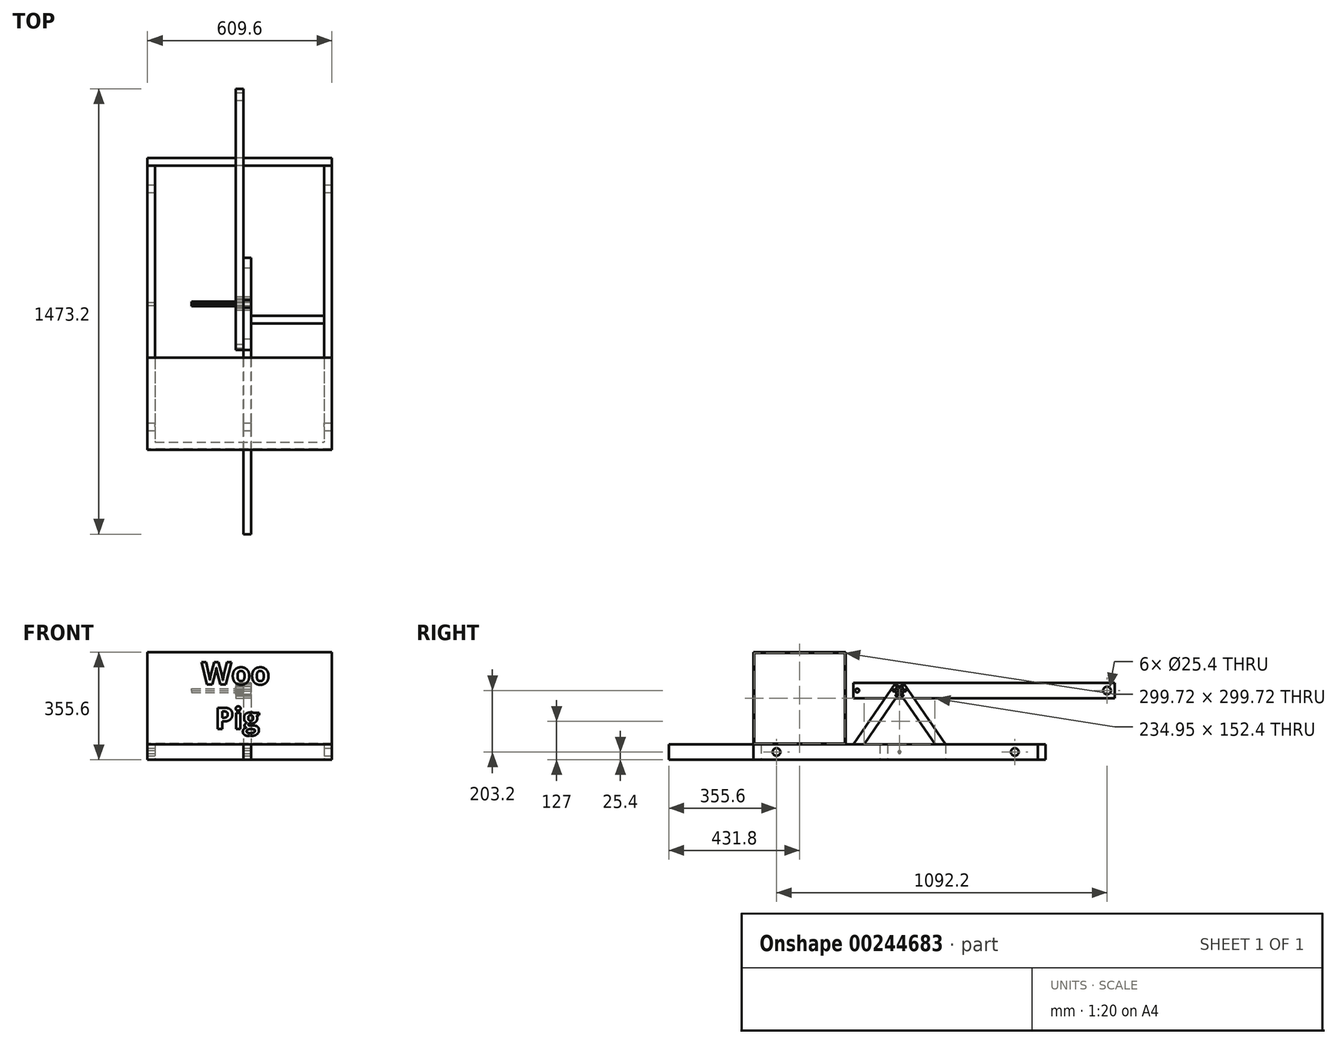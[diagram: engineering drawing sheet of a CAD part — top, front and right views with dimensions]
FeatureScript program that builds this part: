
annotation { "Feature Type Name" : "Feature", "Feature Type Description" : "" }
export const myFeature = defineFeature(function(context is Context, id is Id, definition is map)
    precondition{}
    {
        {
            var Q0;
            Q0=qCreatedBy(makeId("Top.planeOp"),FACE);
            var sketch = newSketch(context, id + "F0", { "sketchPlane" : qUnion([Q0])});
            skLineSegment(sketch, "E0.bottom", {"start": v(0, 863.6) * mm, "end": v(25.4, 863.6) * mm});
            skLineSegment(sketch, "E0.top", {"start": v(0, 0) * mm, "end": v(25.4, 0) * mm});
            skLineSegment(sketch, "E0.left", {"start": v(0, 863.6) * mm, "end": v(0, 0) * mm});
            skLineSegment(sketch, "E0.right", {"start": v(25.4, 863.6) * mm, "end": v(25.4, 0) * mm});
            skSolve(sketch);
        }
        {
            var Q0;
            Q0=makeQuery(id+"F0.imprint","IMPRINT",FACE,{"disambiguationData":[TD([[makeQuery(id+"F0.imprint","IMPRINT",EDGE,{"derivedFrom":sQuery(id+"F0.wireOp",EDGE,"E0.bottom")}),-1.0]])]});
            extrude(context, id + "F1", {"entities" : qUnion([Q0]), "depth" : 50.8 * mm});
        }
        {
            var Q0;
            Q0=makeQuery(id+"F1.opExtrude","SWEPT_FACE",FACE,{"disambiguationData":[OSD([sQuery(id+"F0.wireOp",EDGE,"E0.right")])]});
            var sketch = newSketch(context, id + "F2", { "sketchPlane" : qUnion([Q0])});
            skLineSegment(sketch, "E1", {"start": v(0, 25.4) * mm, "end": v(863.6, 25.4) * mm, "construction": true});
            skCircle(sketch, "E2", {"center": v(152.4, 25.4) * mm, "radius": 12.7 * mm, "construction": true});
            skCircle(sketch, "E3", {"center": v(838.2, 25.4) * mm, "radius": 12.7 * mm});
            skCircle(sketch, "E4", {"center": v(12.7, 25.4) * mm, "radius": 6.35 * mm});
            skSolve(sketch);
        }
        {
            var Q0;
            Q0=qSketchRegion(id+"F2",true);
            extrude(context, id + "F3", {"entities" : qUnion([Q0]), "operationType" : NewBodyOperationType.REMOVE, "endBound" : BoundingType.THROUGH_ALL, "oppositeDirection" : true, "depth" : 25.4 * mm});
        }
        {
            var Q0;
            Q0=makeQuery(id+"F1.opExtrude","SWEPT_FACE",FACE,{"disambiguationData":[OSD([sQuery(id+"F0.wireOp",EDGE,"E0.right")])]});
            var sketch = newSketch(context, id + "F4", { "sketchPlane" : qUnion([Q0])});
            skLineSegment(sketch, "E5", {"start": v(152.4, 50.8) * mm, "end": v(139.7, 50.8) * mm, "construction": true});
            skLineSegment(sketch, "E6", {"start": v(139.7, 50.8) * mm, "end": v(139.7, 0) * mm, "construction": true});
            skLineSegment(sketch, "E7", {"start": v(165.1, 50.8) * mm, "end": v(165.1, 0) * mm, "construction": true});
            skLineSegment(sketch, "E8", {"start": v(139.7, 50.8) * mm, "end": v(0, -152.4) * mm});
            skLineSegment(sketch, "E9", {"start": v(139.7, 0) * mm, "end": v(34.92, -152.4) * mm});
            skLineSegment(sketch, "E10", {"start": v(139.7, 0) * mm, "end": v(139.7, -152.4) * mm, "construction": true});
            skLineSegment(sketch, "E11", {"start": v(139.7, -152.4) * mm, "end": v(-61.1, -152.4) * mm, "construction": true});
            skLineSegment(sketch, "E12", {"start": v(0, -152.4) * mm, "end": v(-609.6, -152.4) * mm});
            skLineSegment(sketch, "E13", {"start": v(-609.6, -152.4) * mm, "end": v(-609.6, -203.2) * mm});
            skLineSegment(sketch, "E14", {"start": v(-609.6, -203.2) * mm, "end": v(139.7, -203.2) * mm});
            skLineSegment(sketch, "E15", {"start": v(34.92, -152.4) * mm, "end": v(139.7, -152.4) * mm});
            skLineSegment(sketch, "E16", {"start": v(152.4, 50.8) * mm, "end": v(152.4, -203.2) * mm, "construction": true});
            skLineSegment(sketch, "E17", {"start": v(139.7, 50.8) * mm, "end": v(152.4, 50.8) * mm});
            skLineSegment(sketch, "E18.MirrorCS", {"start": v(165.1, 0) * mm, "end": v(269.88, -152.4) * mm});
            skLineSegment(sketch, "E19.MirrorCS", {"start": v(165.1, 50.8) * mm, "end": v(304.8, -152.4) * mm});
            skLineSegment(sketch, "E20.MirrorCS", {"start": v(165.1, -152.4) * mm, "end": v(365.9, -152.4) * mm, "construction": true});
            skLineSegment(sketch, "E21.MirrorCS", {"start": v(152.4, 50.8) * mm, "end": v(165.1, 50.8) * mm, "construction": true});
            skLineSegment(sketch, "E22", {"start": v(139.7, -152.4) * mm, "end": v(269.88, -152.4) * mm});
            skLineSegment(sketch, "E23", {"start": v(139.7, -203.2) * mm, "end": v(165.1, -203.2) * mm});
            skLineSegment(sketch, "E24", {"start": v(139.7, 0) * mm, "end": v(165.1, 0) * mm});
            skLineSegment(sketch, "E25", {"start": v(152.4, 50.8) * mm, "end": v(165.1, 50.8) * mm});
            skLineSegment(sketch, "E26", {"start": v(304.8, -152.4) * mm, "end": v(304.8, -203.2) * mm});
            skLineSegment(sketch, "E27", {"start": v(304.8, -203.2) * mm, "end": v(165.1, -203.2) * mm});
            skLineSegment(sketch, "E28", {"start": v(165.1, -152.4) * mm, "end": v(269.88, -152.4) * mm});
            skSolve(sketch);
        }
        {
            var Q0;
            {var subQ0=sQuery(id+"F4.wireOp",EDGE,"E9");Q0=makeQuery(id+"F4.imprint","IMPRINT",FACE,{"disambiguationData":[TD([[makeQuery(id+"F4.imprint","IMPRINT",EDGE,{"derivedFrom":subQ0}),-1.0]])]});}
            var Q1;
            {var subQ7=sQuery(id+"F4.wireOp",EDGE,"E17");Q1=makeQuery(id+"F4.imprint","IMPRINT",FACE,{"disambiguationData":[TD([[makeQuery(id+"F4.imprint","IMPRINT",EDGE,{"derivedFrom":subQ7}),1.0]])]});}
            extrude(context, id + "F5", {"entities" : qUnion([Q0, Q1]), "depth" : 25.4 * mm});
        }
        {
            var Q0;
            Q0=qCreatedBy(makeId("Front.planeOp"),FACE);
            cPlane(context, id + "F6", {"entities" : qUnion([Q0]), "cplaneType" : CPlaneType.OFFSET, "offset" : 304.8 * mm, "width" : 152.4 * mm, "height" : 152.4 * mm});
        }
        {
            var Q0;
            Q0=qCreatedBy(id+"F6.planeOp",FACE);
            var sketch = newSketch(context, id + "F7", { "sketchPlane" : qUnion([Q0])});
            skLineSegment(sketch, "E29", {"start": v(0, 0) * mm, "end": v(0, -319.22) * mm, "construction": true});
            skLineSegment(sketch, "E30", {"start": v(12.7, 0) * mm, "end": v(12.7, -203.2) * mm, "construction": true});
            skLineSegment(sketch, "E31.bottom", {"start": v(-292.1, -152.4) * mm, "end": v(317.5, -152.4) * mm});
            skLineSegment(sketch, "E31.top", {"start": v(-292.1, -203.2) * mm, "end": v(317.5, -203.2) * mm});
            skLineSegment(sketch, "E31.left", {"start": v(-292.1, -152.4) * mm, "end": v(-292.1, -203.2) * mm});
            skLineSegment(sketch, "E31.right", {"start": v(317.5, -152.4) * mm, "end": v(317.5, -203.2) * mm});
            skLineSegment(sketch, "E32", {"start": v(-27.3, -203.2) * mm, "end": v(60.07, -203.2) * mm, "construction": true});
            skSolve(sketch);
        }
        {
            var Q0;
            Q0=makeQuery(id+"F7.imprint","IMPRINT",FACE,{"disambiguationData":[TD([[makeQuery(id+"F7.imprint","IMPRINT",EDGE,{"derivedFrom":sQuery(id+"F7.wireOp",EDGE,"E31.bottom")}),-1.0]])]});
            extrude(context, id + "F8", {"entities" : qUnion([Q0]), "depth" : 25.4 * mm});
        }
        {
            var Q0;
            Q0=makeQuery(id+"F8.opExtrude","CAP_FACE",FACE,{"disambiguationData":[OSD([sQuery(id+"F7.wireOp",EDGE,"E31.bottom"),sQuery(id+"F7.wireOp",EDGE,"E31.top"),sQuery(id+"F7.wireOp",EDGE,"E31.left"),sQuery(id+"F7.wireOp",EDGE,"E31.right")])],"isStart":true});
            var sketch = newSketch(context, id + "F9", { "sketchPlane" : qUnion([Q0])});
            skLineSegment(sketch, "E33.bottom", {"start": v(-317.5, -152.4) * mm, "end": v(-292.1, -152.4) * mm});
            skLineSegment(sketch, "E33.top", {"start": v(-317.5, -203.2) * mm, "end": v(-292.1, -203.2) * mm});
            skLineSegment(sketch, "E33.left", {"start": v(-317.5, -152.4) * mm, "end": v(-317.5, -203.2) * mm});
            skLineSegment(sketch, "E33.right", {"start": v(-292.1, -152.4) * mm, "end": v(-292.1, -203.2) * mm});
            skSolve(sketch);
        }
        {
            var Q0;
            Q0=makeQuery(id+"F9.imprint","IMPRINT",FACE,{"disambiguationData":[TD([[makeQuery(id+"F9.imprint","IMPRINT",EDGE,{"derivedFrom":sQuery(id+"F9.wireOp",EDGE,"E33.bottom")}),1.0]])]});
            extrude(context, id + "F10", {"entities" : qUnion([Q0]), "operationType" : NewBodyOperationType.ADD, "depth" : 914.4 * mm});
        }
        {
            var Q0;
            Q0=makeQuery(id+"F8.opExtrude","CAP_FACE",FACE,{"disambiguationData":[OSD([sQuery(id+"F7.wireOp",EDGE,"E31.bottom"),sQuery(id+"F7.wireOp",EDGE,"E31.top"),sQuery(id+"F7.wireOp",EDGE,"E31.left"),sQuery(id+"F7.wireOp",EDGE,"E31.right")])],"isStart":true});
            var sketch = newSketch(context, id + "F11", { "sketchPlane" : qUnion([Q0])});
            skLineSegment(sketch, "E34.bottom", {"start": v(292.1, -152.4) * mm, "end": v(266.7, -152.4) * mm});
            skLineSegment(sketch, "E34.top", {"start": v(292.1, -203.2) * mm, "end": v(266.7, -203.2) * mm});
            skLineSegment(sketch, "E34.left", {"start": v(292.1, -152.4) * mm, "end": v(292.1, -203.2) * mm});
            skLineSegment(sketch, "E34.right", {"start": v(266.7, -152.4) * mm, "end": v(266.7, -203.2) * mm});
            skSolve(sketch);
        }
        {
            var Q0;
            Q0=makeQuery(id+"F11.imprint","IMPRINT",FACE,{"disambiguationData":[TD([[makeQuery(id+"F11.imprint","IMPRINT",EDGE,{"derivedFrom":sQuery(id+"F11.wireOp",EDGE,"E34.bottom")}),1.0]])]});
            extrude(context, id + "F12", {"entities" : qUnion([Q0]), "operationType" : NewBodyOperationType.ADD, "depth" : 914.4 * mm});
        }
        {
            var Q0;
            Q0=makeQuery(id+"F10.opExtrude","CAP_FACE",FACE,{"disambiguationData":[OSD([sQuery(id+"F9.wireOp",EDGE,"E33.bottom"),sQuery(id+"F9.wireOp",EDGE,"E33.top"),sQuery(id+"F9.wireOp",EDGE,"E33.left"),sQuery(id+"F9.wireOp",EDGE,"E33.right")])],"isStart":false});
            var sketch = newSketch(context, id + "F13", { "sketchPlane" : qUnion([Q0])});
            skLineSegment(sketch, "E35.bottom", {"start": v(-317.5, -152.4) * mm, "end": v(292.1, -152.4) * mm});
            skLineSegment(sketch, "E35.top", {"start": v(-317.5, -203.2) * mm, "end": v(292.1, -203.2) * mm});
            skLineSegment(sketch, "E35.left", {"start": v(-317.5, -152.4) * mm, "end": v(-317.5, -203.2) * mm});
            skLineSegment(sketch, "E35.right", {"start": v(292.1, -152.4) * mm, "end": v(292.1, -203.2) * mm});
            skSolve(sketch);
        }
        {
            var Q0;
            Q0=qSketchRegion(id+"F13",true);
            extrude(context, id + "F14", {"entities" : qUnion([Q0]), "depth" : 25.4 * mm});
        }
        {
            var Q0;
            Q0=makeQuery(id+"F10.boolean.opBoolean","MERGE",FACE,{"derivedFrom":[makeQuery(id+"F8.opExtrude","SWEPT_FACE",FACE,{"disambiguationData":[OSD([sQuery(id+"F7.wireOp",EDGE,"E31.right")])]}),makeQuery(id+"F10.opExtrude","SWEPT_FACE",FACE,{"disambiguationData":[OSD([sQuery(id+"F9.wireOp",EDGE,"E33.left")])]})]});
            var sketch = newSketch(context, id + "F15", { "sketchPlane" : qUnion([Q0])});
            skLineSegment(sketch, "E36.bottom", {"start": v(-330.2, -152.4) * mm, "end": v(609.6, -152.4) * mm, "construction": true});
            skLineSegment(sketch, "E36.top", {"start": v(-330.2, -203.2) * mm, "end": v(609.6, -203.2) * mm, "construction": true});
            skLineSegment(sketch, "E36.left", {"start": v(-330.2, -152.4) * mm, "end": v(-330.2, -203.2) * mm, "construction": true});
            skLineSegment(sketch, "E36.right", {"start": v(609.6, -152.4) * mm, "end": v(609.6, -203.2) * mm, "construction": true});
            skLineSegment(sketch, "E37", {"start": v(609.6, -177.8) * mm, "end": v(-330.2, -177.8) * mm, "construction": true});
            skCircle(sketch, "E38", {"center": v(-254, -177.8) * mm, "radius": 12.7 * mm});
            skLineSegment(sketch, "E39", {"start": v(139.7, -152.4) * mm, "end": v(139.7, -203.2) * mm, "construction": true});
            skCircle(sketch, "E40.MirrorC", {"center": v(533.4, -177.8) * mm, "radius": 12.7 * mm});
            skSolve(sketch);
        }
        {
            var Q0;
            Q0=qSketchRegion(id+"F15",true);
            extrude(context, id + "F16", {"entities" : qUnion([Q0]), "operationType" : NewBodyOperationType.REMOVE, "endBound" : BoundingType.THROUGH_ALL, "oppositeDirection" : true, "depth" : 25.4 * mm});
        }
        {
            var Q0;
            Q0=makeQuery(id+"F12.boolean.opBoolean","MERGE",FACE,{"derivedFrom":[makeQuery(id+"F10.boolean.opBoolean","MERGE",FACE,{"derivedFrom":[makeQuery(id+"F8.opExtrude","SWEPT_FACE",FACE,{"disambiguationData":[OSD([sQuery(id+"F7.wireOp",EDGE,"E31.top")])]}),makeQuery(id+"F10.opExtrude","SWEPT_FACE",FACE,{"disambiguationData":[OSD([sQuery(id+"F9.wireOp",EDGE,"E33.top")])]})]}),makeQuery(id+"F12.opExtrude","SWEPT_FACE",FACE,{"disambiguationData":[OSD([sQuery(id+"F11.wireOp",EDGE,"E34.top")])]})]});
            var sketch = newSketch(context, id + "F17", { "sketchPlane" : qUnion([Q0])});
            skLineSegment(sketch, "E41.bottom", {"start": v(292.1, -87.93) * mm, "end": v(50.8, -87.93) * mm});
            skLineSegment(sketch, "E41.top", {"start": v(292.1, -113.33) * mm, "end": v(50.8, -113.33) * mm});
            skLineSegment(sketch, "E41.left", {"start": v(292.1, -87.93) * mm, "end": v(292.1, -113.33) * mm});
            skLineSegment(sketch, "E41.right", {"start": v(50.8, -87.93) * mm, "end": v(50.8, -113.33) * mm});
            skSolve(sketch);
        }
        {
            var Q0;
            Q0=makeQuery(id+"F17.imprint","IMPRINT",FACE,{"disambiguationData":[TD([[makeQuery(id+"F17.imprint","IMPRINT",EDGE,{"derivedFrom":sQuery(id+"F17.wireOp",EDGE,"E41.bottom")}),1.0]])]});
            extrude(context, id + "F18", {"entities" : qUnion([Q0]), "oppositeDirection" : true, "depth" : 50.8 * mm});
        }
        {
            var Q0;
            Q0=makeQuery(id+"F12.boolean.opBoolean","MERGE",FACE,{"derivedFrom":[makeQuery(id+"F8.opExtrude","SWEPT_FACE",FACE,{"disambiguationData":[OSD([sQuery(id+"F7.wireOp",EDGE,"E31.left")])]}),makeQuery(id+"F12.opExtrude","SWEPT_FACE",FACE,{"disambiguationData":[OSD([sQuery(id+"F11.wireOp",EDGE,"E34.left")])]})]});
            var sketch = newSketch(context, id + "F19", { "sketchPlane" : qUnion([Q0])});
            skLineSegment(sketch, "E42.bottom", {"start": v(330.2, -152.4) * mm, "end": v(25.4, -152.4) * mm});
            skLineSegment(sketch, "E42.top", {"start": v(330.2, 152.4) * mm, "end": v(25.4, 152.4) * mm});
            skLineSegment(sketch, "E42.left", {"start": v(330.2, -152.4) * mm, "end": v(330.2, 152.4) * mm});
            skLineSegment(sketch, "E42.right", {"start": v(25.4, -152.4) * mm, "end": v(25.4, 152.4) * mm});
            skSolve(sketch);
        }
        {
            var Q0;
            Q0=makeQuery(id+"F19.imprint","IMPRINT",FACE,{"disambiguationData":[TD([[makeQuery(id+"F19.imprint","IMPRINT",EDGE,{"derivedFrom":sQuery(id+"F19.wireOp",EDGE,"E42.bottom")}),-1.0]])]});
            extrude(context, id + "F20", {"entities" : qUnion([Q0]), "oppositeDirection" : true, "depth" : 609.6 * mm});
        }
        {
            var Q0;
            Q0=makeQuery(id+"F20.opExtrude","CAP_FACE",FACE,{"disambiguationData":[OSD([sQuery(id+"F19.wireOp",EDGE,"E42.bottom"),sQuery(id+"F19.wireOp",EDGE,"E42.top"),sQuery(id+"F19.wireOp",EDGE,"E42.left"),sQuery(id+"F19.wireOp",EDGE,"E42.right")])],"isStart":true});
            var Q1;
            Q1=makeQuery(id+"F20.opExtrude","CAP_FACE",FACE,{"disambiguationData":[OSD([sQuery(id+"F19.wireOp",EDGE,"E42.bottom"),sQuery(id+"F19.wireOp",EDGE,"E42.top"),sQuery(id+"F19.wireOp",EDGE,"E42.left"),sQuery(id+"F19.wireOp",EDGE,"E42.right")])],"isStart":false});
            shell(context, id + "F21", {"entities" : qUnion([Q0, Q1]), "thickness" : 2.54 * mm});
        }
        {
            var Q0;
            Q0=makeQuery(id+"F20.opExtrude","SWEPT_FACE",FACE,{"disambiguationData":[OSD([sQuery(id+"F19.wireOp",EDGE,"E42.left")])]});
            var sketch = newSketch(context, id + "F22", { "sketchPlane" : qUnion([Q0])});
            skText(sketch, "E43", { "text": "Woo", "fontName": "OpenSans-Bold.ttf"});
            skText(sketch, "E44", { "text": "Pig", "fontName": "OpenSans-Bold.ttf"});
            const initialGuessF22  = {"E43": [-0.1139, 0.04534, 1, 0, 0.07397], "E44": [-0.06886, -0.1016, 1, 0, 0.07074]};
            skSetInitialGuess(sketch, initialGuessF22);
            skSolve(sketch);
        }
        {
            var Q0;
            Q0=qSketchRegion(id+"F22",true);
            extrude(context, id + "F23", {"entities" : qUnion([Q0]), "operationType" : NewBodyOperationType.REMOVE, "oppositeDirection" : true, "depth" : 1.27 * mm});
        }
        {
            var Q0;
            Q0=makeQuery(id+"F5.opExtrude","SWEPT_BODY",BODY,{"disambiguationData":[OSD([sQuery(id+"F2.wireOp",EDGE,"E2"),sQuery(id+"F4.wireOp",EDGE,"E8"),sQuery(id+"F4.wireOp",EDGE,"E9"),sQuery(id+"F4.wireOp",EDGE,"E12"),sQuery(id+"F4.wireOp",EDGE,"E13"),sQuery(id+"F4.wireOp",EDGE,"E14"),sQuery(id+"F4.wireOp",EDGE,"E15"),sQuery(id+"F4.wireOp",EDGE,"E17"),sQuery(id+"F4.wireOp",EDGE,"E18.MirrorCS"),sQuery(id+"F4.wireOp",EDGE,"E19.MirrorCS"),sQuery(id+"F4.wireOp",EDGE,"E22"),sQuery(id+"F4.wireOp",EDGE,"E23"),sQuery(id+"F4.wireOp",EDGE,"E24"),sQuery(id+"F4.wireOp",EDGE,"E25"),sQuery(id+"F4.wireOp",EDGE,"E26"),sQuery(id+"F4.wireOp",EDGE,"E27"),sQuery(id+"F4.wireOp",EDGE,"E28")])]});
            transform(context, id + "F24", {"entities" : qUnion([Q0]), "transformType" : TransformType.TRANSLATION_3D, "dx" : 0 * mm, "dy" : 0 * mm, "dz" : 0 * mm, "makeCopy" : true});
        }
        {
            var Q0;
            Q0=makeQuery(id+"F24.opPattern","COPY",BODY,{"derivedFrom":makeQuery(id+"F5.opExtrude","SWEPT_BODY",BODY,{"disambiguationData":[OSD([sQuery(id+"F2.wireOp",EDGE,"E2"),sQuery(id+"F4.wireOp",EDGE,"E8"),sQuery(id+"F4.wireOp",EDGE,"E9"),sQuery(id+"F4.wireOp",EDGE,"E12"),sQuery(id+"F4.wireOp",EDGE,"E13"),sQuery(id+"F4.wireOp",EDGE,"E14"),sQuery(id+"F4.wireOp",EDGE,"E15"),sQuery(id+"F4.wireOp",EDGE,"E17"),sQuery(id+"F4.wireOp",EDGE,"E18.MirrorCS"),sQuery(id+"F4.wireOp",EDGE,"E19.MirrorCS"),sQuery(id+"F4.wireOp",EDGE,"E22"),sQuery(id+"F4.wireOp",EDGE,"E23"),sQuery(id+"F4.wireOp",EDGE,"E24"),sQuery(id+"F4.wireOp",EDGE,"E25"),sQuery(id+"F4.wireOp",EDGE,"E26"),sQuery(id+"F4.wireOp",EDGE,"E27"),sQuery(id+"F4.wireOp",EDGE,"E28")])]}),"instanceName":"1"});
            deleteBodies(context, id + "F25", {"entities" : qUnion([Q0])});
        }
        {
            var Q0;
            Q0=makeQuery(id+"F5.opExtrude","CAP_FACE",FACE,{"disambiguationData":[OSD([sQuery(id+"F4.wireOp",EDGE,"E8"),sQuery(id+"F4.wireOp",EDGE,"E9"),sQuery(id+"F4.wireOp",EDGE,"E12"),sQuery(id+"F4.wireOp",EDGE,"E13"),sQuery(id+"F4.wireOp",EDGE,"E14"),sQuery(id+"F4.wireOp",EDGE,"E15"),sQuery(id+"F4.wireOp",EDGE,"E17"),sQuery(id+"F4.wireOp",EDGE,"E18.MirrorCS"),sQuery(id+"F4.wireOp",EDGE,"E19.MirrorCS"),sQuery(id+"F4.wireOp",EDGE,"E22"),sQuery(id+"F4.wireOp",EDGE,"E23"),sQuery(id+"F4.wireOp",EDGE,"E24"),sQuery(id+"F4.wireOp",EDGE,"E25"),sQuery(id+"F4.wireOp",EDGE,"E26"),sQuery(id+"F4.wireOp",EDGE,"E27"),sQuery(id+"F4.wireOp",EDGE,"E28")])],"isStart":false});
            var sketch = newSketch(context, id + "F26", { "sketchPlane" : qUnion([Q0])});
            skLineSegment(sketch, "E45", {"start": v(139.7, 50.8) * mm, "end": v(139.7, 0) * mm, "construction": true});
            skLineSegment(sketch, "E46", {"start": v(139.7, 0) * mm, "end": v(165.1, 0) * mm, "construction": true});
            skLineSegment(sketch, "E47", {"start": v(165.1, 0) * mm, "end": v(165.1, 50.8) * mm, "construction": true});
            skLineSegment(sketch, "E48", {"start": v(165.1, 50.8) * mm, "end": v(139.7, 50.8) * mm, "construction": true});
            skLineSegment(sketch, "E49", {"start": v(139.7, 25.4) * mm, "end": v(165.1, 25.4) * mm, "construction": true});
            skCircle(sketch, "E50", {"center": v(152.4, 25.4) * mm, "radius": 14.02 * mm});
            skSolve(sketch);
        }
        {
            var Q0;
            Q0=makeQuery(id+"F26.imprint","IMPRINT",FACE,{"disambiguationData":[TD([[makeQuery(id+"F26.imprint","IMPRINT",EDGE,{"derivedFrom":sQuery(id+"F26.wireOp",EDGE,"E50")}),1.0]])]});
            var Q1;
            Q1=makeQuery(id+"F5.opExtrude","CAP_FACE",FACE,{"disambiguationData":[OSD([sQuery(id+"F4.wireOp",EDGE,"E8"),sQuery(id+"F4.wireOp",EDGE,"E9"),sQuery(id+"F4.wireOp",EDGE,"E12"),sQuery(id+"F4.wireOp",EDGE,"E13"),sQuery(id+"F4.wireOp",EDGE,"E14"),sQuery(id+"F4.wireOp",EDGE,"E15"),sQuery(id+"F4.wireOp",EDGE,"E17"),sQuery(id+"F4.wireOp",EDGE,"E18.MirrorCS"),sQuery(id+"F4.wireOp",EDGE,"E19.MirrorCS"),sQuery(id+"F4.wireOp",EDGE,"E22"),sQuery(id+"F4.wireOp",EDGE,"E23"),sQuery(id+"F4.wireOp",EDGE,"E24"),sQuery(id+"F4.wireOp",EDGE,"E25"),sQuery(id+"F4.wireOp",EDGE,"E26"),sQuery(id+"F4.wireOp",EDGE,"E27"),sQuery(id+"F4.wireOp",EDGE,"E28")])],"isStart":true});
            extrude(context, id + "F27", {"entities" : qUnion([Q0]), "operationType" : NewBodyOperationType.REMOVE, "endBound" : BoundingType.UP_TO_SURFACE, "oppositeDirection" : true, "endBoundEntityFace" : qUnion([Q1]), "depth" : 25.4 * mm});
        }
        {
            var Q0;
            Q0=makeQuery(id+"F1.opExtrude","SWEPT_FACE",FACE,{"disambiguationData":[OSD([sQuery(id+"F0.wireOp",EDGE,"E0.right")])]});
            var sketch = newSketch(context, id + "F28", { "sketchPlane" : qUnion([Q0])});
            skLineSegment(sketch, "E51", {"start": v(139.7, 50.8) * mm, "end": v(139.7, 0) * mm, "construction": true});
            skCircle(sketch, "E52", {"center": v(152.4, 25.4) * mm, "radius": 14.02 * mm, "construction": true});
            skCircle(sketch, "E53.cCircle", {"center": v(152.4, 25.4) * mm, "radius": 6.35 * mm, "construction": true});
            skLineSegment(sketch, "E53.0", {"start": v(156.07, 19.05) * mm, "end": v(148.73, 19.05) * mm});
            skLineSegment(sketch, "E53.1", {"start": v(148.73, 19.05) * mm, "end": v(145.07, 25.4) * mm});
            skLineSegment(sketch, "E53.2", {"start": v(145.07, 25.4) * mm, "end": v(148.73, 31.75) * mm});
            skLineSegment(sketch, "E53.3", {"start": v(148.73, 31.75) * mm, "end": v(156.07, 31.75) * mm});
            skLineSegment(sketch, "E53.4", {"start": v(156.07, 31.75) * mm, "end": v(159.73, 25.4) * mm});
            skLineSegment(sketch, "E53.5", {"start": v(159.73, 25.4) * mm, "end": v(156.07, 19.05) * mm});
            skPoint(sketch, "E53.0.midPoint", {"position": v(152.4, 19.05) * mm});
            skSolve(sketch);
        }
        {
            var Q0;
            Q0=makeQuery(id+"F28.imprint","IMPRINT",FACE,{"disambiguationData":[TD([[makeQuery(id+"F28.imprint","IMPRINT",EDGE,{"derivedFrom":sQuery(id+"F28.wireOp",EDGE,"E53.0")}),-1.0]])]});
            extrude(context, id + "F29", {"entities" : qUnion([Q0]), "operationType" : NewBodyOperationType.REMOVE, "endBound" : BoundingType.THROUGH_ALL, "oppositeDirection" : true, "depth" : 25.4 * mm});
        }
        {
            var Q0;
            Q0=makeQuery(id+"F1.opExtrude","SWEPT_FACE",FACE,{"disambiguationData":[OSD([sQuery(id+"F0.wireOp",EDGE,"E0.left")])]});
            var sketch = newSketch(context, id + "F30", { "sketchPlane" : qUnion([Q0])});
            skCircle(sketch, "E54.cCircle", {"center": v(-152.4, 25.4) * mm, "radius": 6.35 * mm, "construction": true});
            skPoint(sketch, "E54.cCircle.centerSnap0", {"position": v(-152.4, 19.05) * mm});
            skLineSegment(sketch, "E54.0", {"start": v(-148.73, 19.05) * mm, "end": v(-156.07, 19.05) * mm});
            skLineSegment(sketch, "E54.1", {"start": v(-156.07, 19.05) * mm, "end": v(-159.73, 25.4) * mm});
            skLineSegment(sketch, "E54.2", {"start": v(-159.73, 25.4) * mm, "end": v(-156.07, 31.75) * mm});
            skLineSegment(sketch, "E54.3", {"start": v(-156.07, 31.75) * mm, "end": v(-148.73, 31.75) * mm});
            skLineSegment(sketch, "E54.4", {"start": v(-148.73, 31.75) * mm, "end": v(-145.07, 25.4) * mm});
            skLineSegment(sketch, "E54.5", {"start": v(-145.07, 25.4) * mm, "end": v(-148.73, 19.05) * mm});
            skPoint(sketch, "E54.0.midPoint", {"position": v(-152.4, 19.05) * mm});
            skSolve(sketch);
        }
        {
            var Q0;
            Q0=makeQuery(id+"F30.imprint","IMPRINT",FACE,{"disambiguationData":[TD([[makeQuery(id+"F30.imprint","IMPRINT",EDGE,{"derivedFrom":sQuery(id+"F30.wireOp",EDGE,"E54.0")}),1.0]])]});
            extrude(context, id + "F31", {"entities" : qUnion([Q0]), "depth" : 146.05 * mm});
        }
        {
            var Q0;
            Q0=makeQuery(id+"F1.opExtrude","SWEPT_FACE",FACE,{"disambiguationData":[OSD([sQuery(id+"F0.wireOp",EDGE,"E0.left")])]});
            var sketch = newSketch(context, id + "F32", { "sketchPlane" : qUnion([Q0])});
            skLineSegment(sketch, "E55", {"start": v(-145.07, 25.4) * mm, "end": v(-117.53, 25.4) * mm, "construction": true});
            skLineSegment(sketch, "E56", {"start": v(-152.4, 31.75) * mm, "end": v(-152.4, 19.05) * mm, "construction": true});
            skCircle(sketch, "E57", {"center": v(-133.35, 25.4) * mm, "radius": 3.18 * mm});
            skPoint(sketch, "E58", {"position": v(-152.4, 25.4) * mm});
            skCircle(sketch, "E59", {"center": v(-152.4, 25.4) * mm, "radius": 28.58 * mm, "construction": true});
            skCircle(sketch, "E60.1.0", {"center": v(-142.88, 41.9) * mm, "radius": 3.18 * mm});
            skCircle(sketch, "E60.2.0", {"center": v(-161.93, 41.9) * mm, "radius": 3.18 * mm});
            skCircle(sketch, "E60.3.0", {"center": v(-171.45, 25.4) * mm, "radius": 3.18 * mm});
            skCircle(sketch, "E60.4.0", {"center": v(-161.92, 8.9) * mm, "radius": 3.18 * mm});
            skCircle(sketch, "E60.5.0", {"center": v(-142.87, 8.9) * mm, "radius": 3.18 * mm});
            skSolve(sketch);
        }
        {
            var Q0;
            Q0 = qSketchRegion(id + "F32", true);
            extrude(context, id + "F33", {"entities" : qUnion([Q0]), "operationType" : NewBodyOperationType.REMOVE, "oppositeDirection" : true, "depth" : 50.8 * mm});
        }
        {
            var Q0;
            Q0=makeQuery(id+"F5.opExtrude","CAP_FACE",FACE,{"disambiguationData":[OSD([sQuery(id+"F4.wireOp",EDGE,"E8"),sQuery(id+"F4.wireOp",EDGE,"E9"),sQuery(id+"F4.wireOp",EDGE,"E12"),sQuery(id+"F4.wireOp",EDGE,"E13"),sQuery(id+"F4.wireOp",EDGE,"E14"),sQuery(id+"F4.wireOp",EDGE,"E15"),sQuery(id+"F4.wireOp",EDGE,"E17"),sQuery(id+"F4.wireOp",EDGE,"E18.MirrorCS"),sQuery(id+"F4.wireOp",EDGE,"E19.MirrorCS"),sQuery(id+"F4.wireOp",EDGE,"E22"),sQuery(id+"F4.wireOp",EDGE,"E23"),sQuery(id+"F4.wireOp",EDGE,"E24"),sQuery(id+"F4.wireOp",EDGE,"E25"),sQuery(id+"F4.wireOp",EDGE,"E26"),sQuery(id+"F4.wireOp",EDGE,"E27"),sQuery(id+"F4.wireOp",EDGE,"E28")])],"isStart":false});
            var sketch = newSketch(context, id + "F34", { "sketchPlane" : qUnion([Q0])});
            skLineSegment(sketch, "E61", {"start": v(139.7, 50.8) * mm, "end": v(139.7, -203.2) * mm, "construction": true});
            skLineSegment(sketch, "E62", {"start": v(165.1, 50.8) * mm, "end": v(165.1, -203.2) * mm, "construction": true});
            skLineSegment(sketch, "E63", {"start": v(152.4, -152.4) * mm, "end": v(152.4, -203.2) * mm, "construction": true});
            skPoint(sketch, "E64", {"position": v(152.4, -177.8) * mm});
            skCircle(sketch, "E65", {"center": v(152.4, -177.8) * mm, "radius": 4.76 * mm});
            skSolve(sketch);
        }
        {
            var Q0;
            Q0 = qSketchRegion(id + "F34", true);
            extrude(context, id + "F35", {"entities" : qUnion([Q0]), "operationType" : NewBodyOperationType.REMOVE, "endBound" : BoundingType.THROUGH_ALL, "oppositeDirection" : true, "depth" : 25.4 * mm});
        }
    });
